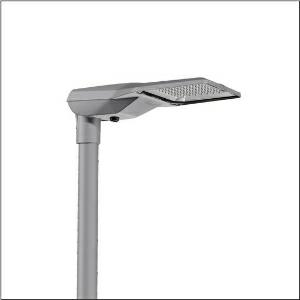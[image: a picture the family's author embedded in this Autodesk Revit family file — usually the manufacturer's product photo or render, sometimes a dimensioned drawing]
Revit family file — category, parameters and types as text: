
# Revit family: streetlight_sl_21_iq_midi___p0_8ab_5xe3r31u08mb_57c5
name_source: partatom
category: Lighting Fixtures
units: mm (PartAtom-declared; Revit-internal decimal feet)

## family parameters
Cut with Voids When Loaded = No
Host = Face
Light Source = No
Part Type = Normal
Room Calculation Point = No
Round Connector Dimension = Use Diameter
Shared = No

## types (1)
- --- (1 x LED, 15920 lm, 129.3 W, 3000K)
    Apparent Load = 129 VA
    CIE Flux Codes = 36 71 98 100 100
    Color Rendering = 70
    Color Temperature = 3000K
    Default Elevation = 1800 mm
    Description = Streetlight SL 21 iQ midi, mast luminaire, primary light control with lens, of PMMA, primary optical cover: cover, of toughened safety glass, transparent, light distribution: P0.8aB, light emission: direct distribution, primary light characteristic: asymmetric, installation type: post-top, side-entry, LED, High Power LED, rated luminous flux: 15.920lm, luminous efficacy: 123lm/W, light colour: 730, colour temperature: 3000K, control gear: iQ-Street Remote, D4i with power reduction, control: pre-setting: logarithmic dimming characteristic, Street-Remote, Auto-Match, Temp-Guard, Lumen-Switch, Night-Set, Smart-Wire, Light-Fading, Desk-Remote (wireless, voltage-free reading and setting of iQ features in the workshop via application-optimized NFC function/RFID function), optimised constant luminous flux control (CLO 2.0), mains connection: 230..240V, AC, 50/60Hz, start of lifetime: 129W, end of service life: 142W, reduction: 56W, luminaire housing, of diecast aluminium, powder-coated, Siteco® metallic grey (DB 702S), corrosivity category C5 mid according to DIN EN ISO 12944, please order mast flange separately, inclination adjustable: 0°, 5°, 10°, 15°, sealing non-destructively replaceable, multi-level sealing system, length: 644mm, width: 335mm, height: 110mm, mast flange for spigot size: 42mm (side-entry): 5XC10008XM4, 60/48mm (side-entry/post-top): 5XC10108XM2, 76/60mm (side-entry/post-top): 5XC10108XM1, mounting height: 4..8m, Smart Interface below, protection rating (complete): IP66, insulation class (complete): insulation class II (safety insulation), certification: CE, ENEC, ENEC+, VDE, impact resistance: IK10, permissible operating ambient temperature for outdoor applications: -40..+50°C, standard-compliant lighting for roads and squares, packaging unit: 1 piece

Light Distribution: P0.8aB
    Height = 111 mm
    Lamp = 1 x LED
    Lamp Light Flux = 15920 lm
    Lamp Power = 129.3 W
    Lamp count = 1
    Length = 644 mm
    Luminous efficacy = 123 lm/W
    Manufacturer = Siteco
    ModVariant = No
    Model = 5XE3R31U08MB
    Number of Poles = 1
    OnlyDefault = Yes
    Power Factor = 1
    Product Name = Streetlight SL 21 iQ midi | P0.8aB
    Product group = mast luminaire | pylon top
    ProductGroupID = 6100
    Protection Class = Protection class II
    Protection Degree = IP 66
    RLX_Detail_Level = 1
    RLX_Emergency_Light_Flux = 0 lm
    RLX_Emergency_Type = 0
    RLX_Emergency_Type_DB = No
    RlxData = <blob elided: 90705 chars, md5=bc8f833a>
    Socket = socket
    Standby Power = 0 W
    System Light Flux = 15919 lm
    System Power = 129 W
    Type Comments = factory setting: luminous flux: 100 % | dim-lin: 254 | 672 mA
    Type Image = l_1004300.jpg
    URL = http://relux.com
    VarID = @adj_096795
    Voltage = 0 V
    Weight = 0.00 kg
    Width = 336 mm

## geometry (parser evidence)
native form markers: Blend x4, Sweep x11
no freeform markers — native parametric forms only
